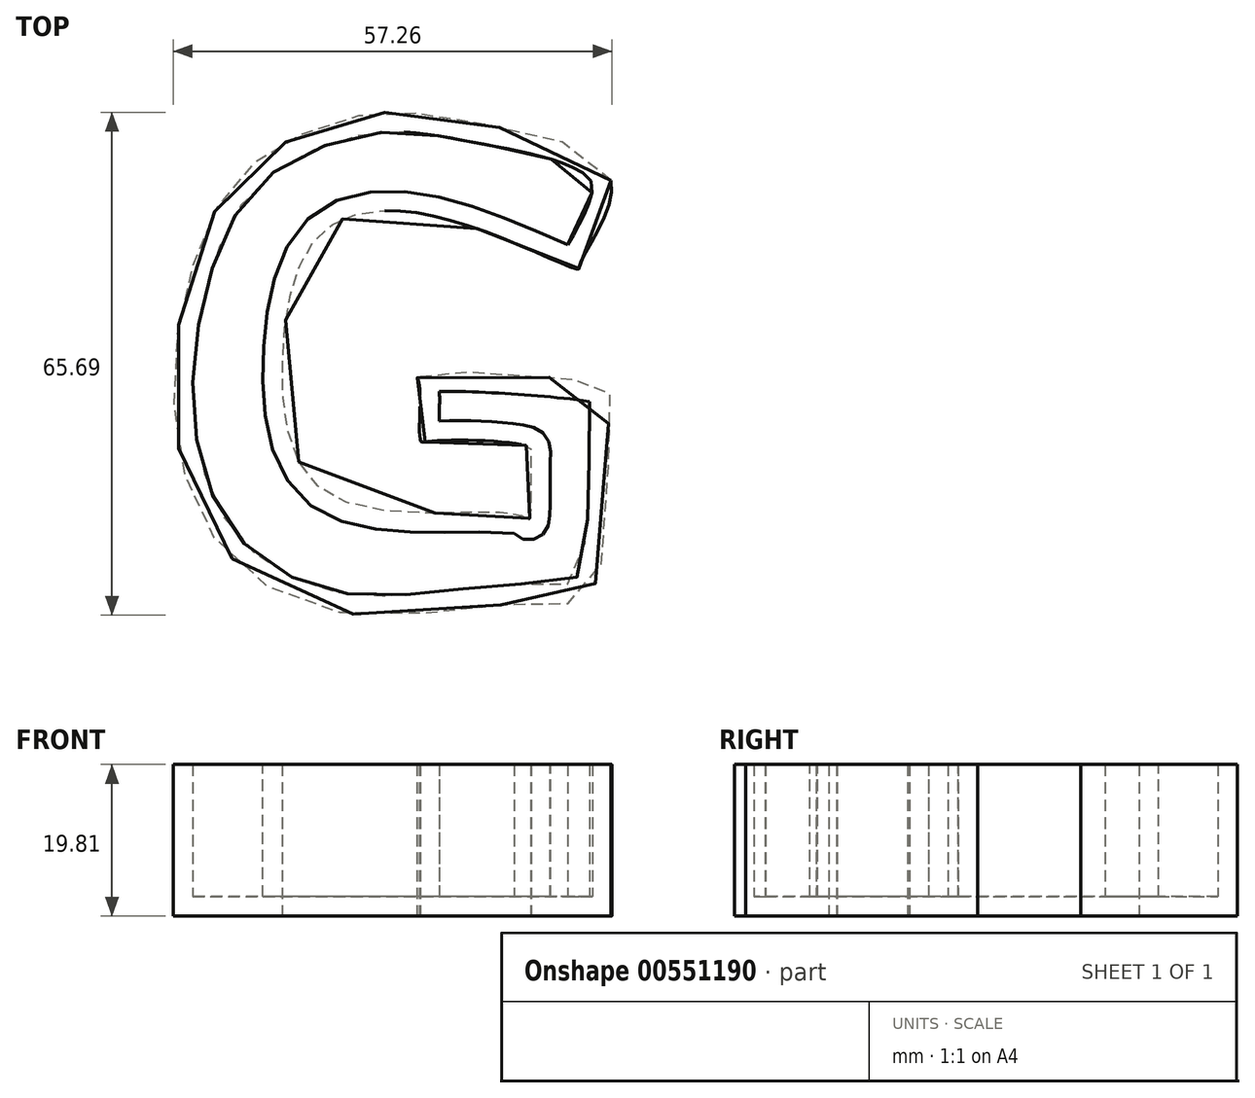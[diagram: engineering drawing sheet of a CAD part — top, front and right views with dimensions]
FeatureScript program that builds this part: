
annotation { "Feature Type Name" : "Feature", "Feature Type Description" : "" }
export const myFeature = defineFeature(function(context is Context, id is Id, definition is map)
    precondition{}
    {
        {
            var Q0;
            Q0=qCreatedBy(makeId("Top.planeOp"),FACE);
            var sketch = newSketch(context, id + "F0", { "sketchPlane" : qUnion([Q0])});
            skFitSpline(sketch, "E0", {"points": [v(29.98, 39.72) * mm, v(14.24, 46.84) * mm, v(0, 48.53) * mm, v(-11.62, 45.16) * mm, v(-20.05, 38.41) * mm, v(-25.67, 24.92) * mm, v(-26.98, 8.06) * mm, v(-21.17, -7.87) * mm, v(-4.3, -16.86) * mm, v(18.93, -15.55) * mm, v(27.73, -13.3) * mm, v(29.8, 11.43) * mm, v(29.42, 12.93) * mm, v(4.87, 14.43) * mm, v(4.87, 13.3) * mm, v(5.06, 5.8) * mm, v(6.37, 5.62) * mm, v(18.93, 5.06) * mm, v(19.49, 3.56) * mm, v(19.3, -4.68) * mm, v(18.36, -4.12) * mm, v(-5.8, -1.87) * mm, v(-12.93, 16.11) * mm, v(-7.5, 33.17) * mm, v(9.74, 34.3) * mm, v(25.67, 28.1) * mm, v(25.86, 28.67) * mm, v(29.98, 39.72) * mm]});
            skSolve(sketch);
        }
        {
            var Q0;
            Q0=makeQuery(id+"F0.imprint","IMPRINT",FACE,{"disambiguationData":[TD([[makeQuery(id+"F0.imprint","IMPRINT",EDGE,{"derivedFrom":sQuery(id+"F0.wireOp",EDGE,"E0")}),1.0]])]});
            extrude(context, id + "F1", {"entities" : qUnion([Q0]), "depth" : 19.8 * mm, "offsetDistance" : 25.4 * mm});
        }
        {
            var Q0;
            Q0=makeQuery(id+"F1.opExtrude","CAP_FACE",FACE,{"disambiguationData":[OSD([sQuery(id+"F0.wireOp",EDGE,"E0")])],"isStart":false});
            shell(context, id + "F2", {"entities" : qUnion([Q0]), "thickness" : 2.54 * mm});
        }
    });
